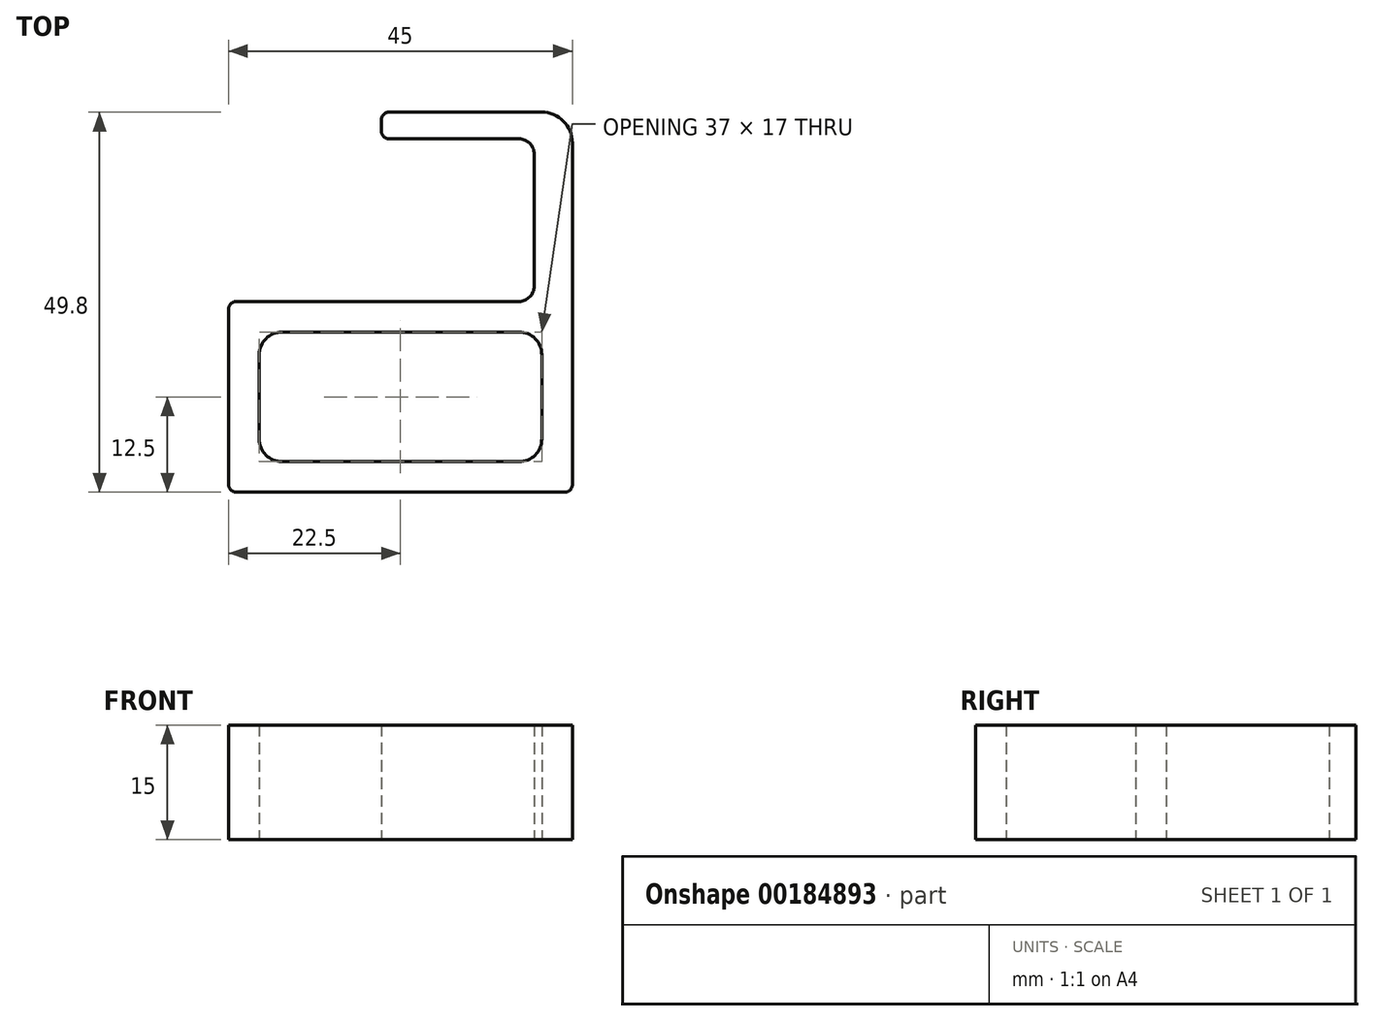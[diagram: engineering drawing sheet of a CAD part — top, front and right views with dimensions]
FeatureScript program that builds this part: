
annotation { "Feature Type Name" : "Feature", "Feature Type Description" : "" }
export const myFeature = defineFeature(function(context is Context, id is Id, definition is map)
    precondition{}
    {
        {
            var Q0;
            Q0=qCreatedBy(makeId("Top.planeOp"),FACE);
            var sketch = newSketch(context, id + "F0", { "sketchPlane" : qUnion([Q0])});
            skLineSegment(sketch, "E0", {"start": v(0, 0) * mm, "end": v(-19, 0) * mm});
            skLineSegment(sketch, "E1", {"start": v(-20, -1) * mm, "end": v(-20, -2.5) * mm});
            skLineSegment(sketch, "E2", {"start": v(-19, -3.5) * mm, "end": v(-2, -3.5) * mm});
            skLineSegment(sketch, "E3", {"start": v(0, -5.5) * mm, "end": v(0, -22.8) * mm});
            skLineSegment(sketch, "E4", {"start": v(-2, -24.8) * mm, "end": v(-39, -24.8) * mm});
            skLineSegment(sketch, "E5", {"start": v(-40, -25.8) * mm, "end": v(-40, -48.8) * mm});
            skLineSegment(sketch, "E6", {"start": v(-39, -49.8) * mm, "end": v(4, -49.8) * mm});
            skLineSegment(sketch, "E7", {"start": v(5, -48.8) * mm, "end": v(5, -4) * mm});
            skLineSegment(sketch, "E8", {"start": v(1, 0) * mm, "end": v(0, 0) * mm});
            skPoint(sketch, "E9.visualSharp", {"position": v(5, 0) * mm});
            skArc(sketch, "E9.filletArc", {"start": v(5, -4) * mm, "mid": v(3.83, -1.17) * mm, "end": v(1, 0) * mm});
            skPoint(sketch, "E10.visualSharp", {"position": v(-20, 0) * mm});
            skArc(sketch, "E10.filletArc", {"start": v(-19, 0) * mm, "mid": v(-19.7, -0.3) * mm, "end": v(-20, -1) * mm});
            skPoint(sketch, "E11.visualSharp", {"position": v(-20, -3.5) * mm});
            skArc(sketch, "E11.filletArc", {"start": v(-20, -2.5) * mm, "mid": v(-19.7, -3.2) * mm, "end": v(-19, -3.5) * mm});
            skPoint(sketch, "E12.visualSharp", {"position": v(0, -3.5) * mm});
            skArc(sketch, "E12.filletArc", {"start": v(0, -5.5) * mm, "mid": v(-0.59, -4.09) * mm, "end": v(-2, -3.5) * mm});
            skPoint(sketch, "E13.visualSharp", {"position": v(0, -24.8) * mm});
            skArc(sketch, "E13.filletArc", {"start": v(-2, -24.8) * mm, "mid": v(-0.59, -24.21) * mm, "end": v(0, -22.8) * mm});
            skPoint(sketch, "E14.visualSharp", {"position": v(-40, -49.8) * mm});
            skArc(sketch, "E14.filletArc", {"start": v(-40, -48.8) * mm, "mid": v(-39.7, -49.5) * mm, "end": v(-39, -49.8) * mm});
            skPoint(sketch, "E15.visualSharp", {"position": v(5, -49.8) * mm});
            skArc(sketch, "E15.filletArc", {"start": v(4, -49.8) * mm, "mid": v(4.7, -49.5) * mm, "end": v(5, -48.8) * mm});
            skPoint(sketch, "E16.visualSharp", {"position": v(-40, -24.8) * mm});
            skArc(sketch, "E16.filletArc", {"start": v(-39, -24.8) * mm, "mid": v(-39.7, -25.1) * mm, "end": v(-40, -25.8) * mm});
            skLineSegment(sketch, "E17", {"start": v(-33, -28.8) * mm, "end": v(-2, -28.8) * mm});
            skLineSegment(sketch, "E18", {"start": v(1, -31.8) * mm, "end": v(1, -42.8) * mm});
            skLineSegment(sketch, "E19", {"start": v(-2, -45.8) * mm, "end": v(-33, -45.8) * mm});
            skLineSegment(sketch, "E20", {"start": v(-36, -42.8) * mm, "end": v(-36, -31.8) * mm});
            skPoint(sketch, "E21.visualSharp", {"position": v(-36, -28.8) * mm});
            skArc(sketch, "E21.filletArc", {"start": v(-33, -28.8) * mm, "mid": v(-35.12, -29.68) * mm, "end": v(-36, -31.8) * mm});
            skPoint(sketch, "E22.visualSharp", {"position": v(-36, -45.8) * mm});
            skArc(sketch, "E22.filletArc", {"start": v(-36, -42.8) * mm, "mid": v(-35.12, -44.92) * mm, "end": v(-33, -45.8) * mm});
            skPoint(sketch, "E23.visualSharp", {"position": v(1, -28.8) * mm});
            skArc(sketch, "E23.filletArc", {"start": v(1, -31.8) * mm, "mid": v(0.12, -29.68) * mm, "end": v(-2, -28.8) * mm});
            skPoint(sketch, "E24.visualSharp", {"position": v(1, -45.8) * mm});
            skArc(sketch, "E24.filletArc", {"start": v(-2, -45.8) * mm, "mid": v(0.12, -44.92) * mm, "end": v(1, -42.8) * mm});
            skSolve(sketch);
        }
        {
            var Q0;
            Q0=makeQuery(id+"F0.imprint","IMPRINT",FACE,{"disambiguationData":[TD([[makeQuery(id+"F0.imprint","IMPRINT",EDGE,{"derivedFrom":sQuery(id+"F0.wireOp",EDGE,"E0")}),1.0]])]});
            extrude(context, id + "F1", {"entities" : qUnion([Q0]), "depth" : 15 * mm});
        }
    });
